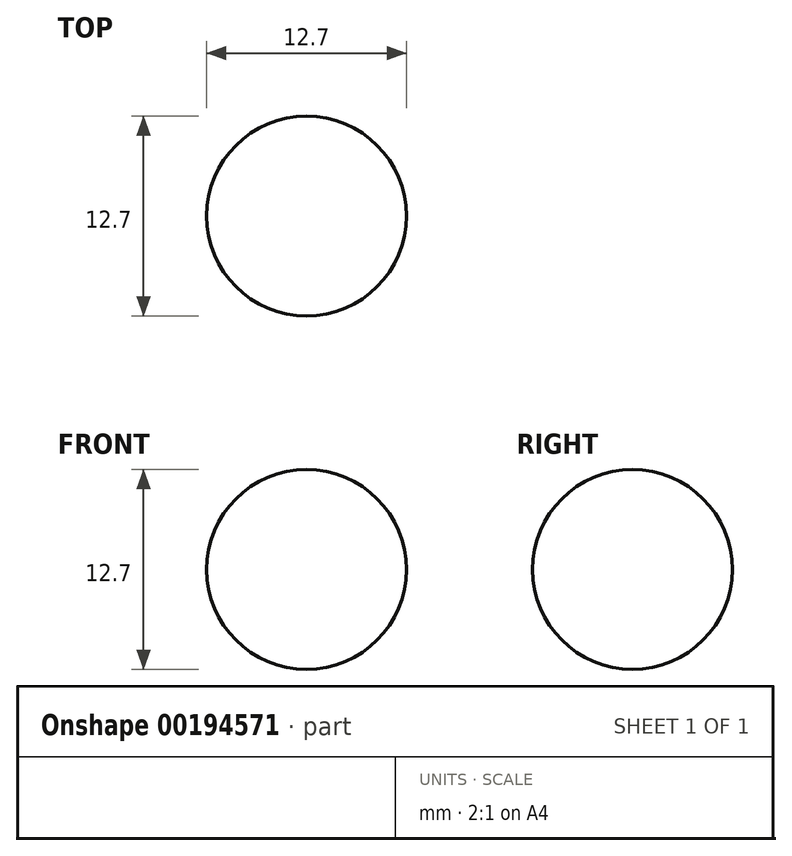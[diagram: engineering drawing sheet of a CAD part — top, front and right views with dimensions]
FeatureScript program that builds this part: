
annotation { "Feature Type Name" : "Feature", "Feature Type Description" : "" }
export const myFeature = defineFeature(function(context is Context, id is Id, definition is map)
    precondition{}
    {
        {
            var Q0;
            Q0=qCreatedBy(makeId("Front.planeOp"),FACE);
            var sketch = newSketch(context, id + "F0", { "sketchPlane" : qUnion([Q0])});
            skArc(sketch, "E0", {"start": v(0, -6.35) * mm, "mid": v(6.35, 0) * mm, "end": v(0, 6.35) * mm});
            skLineSegment(sketch, "E1", {"start": v(0, 6.35) * mm, "end": v(0, -6.35) * mm});
            skSolve(sketch);
        }
        {
            var Q0;
            Q0 = qSketchRegion(id + "F0", true);
            var Q1;
            Q1=sQuery(id+"F0.wireOp",EDGE,"E1");
            revolve(context, id + "F1", {"entities" : qUnion([Q0]), "axis" : qUnion([Q1]), "revolveType" : RevolveType.FULL});
        }
    });
